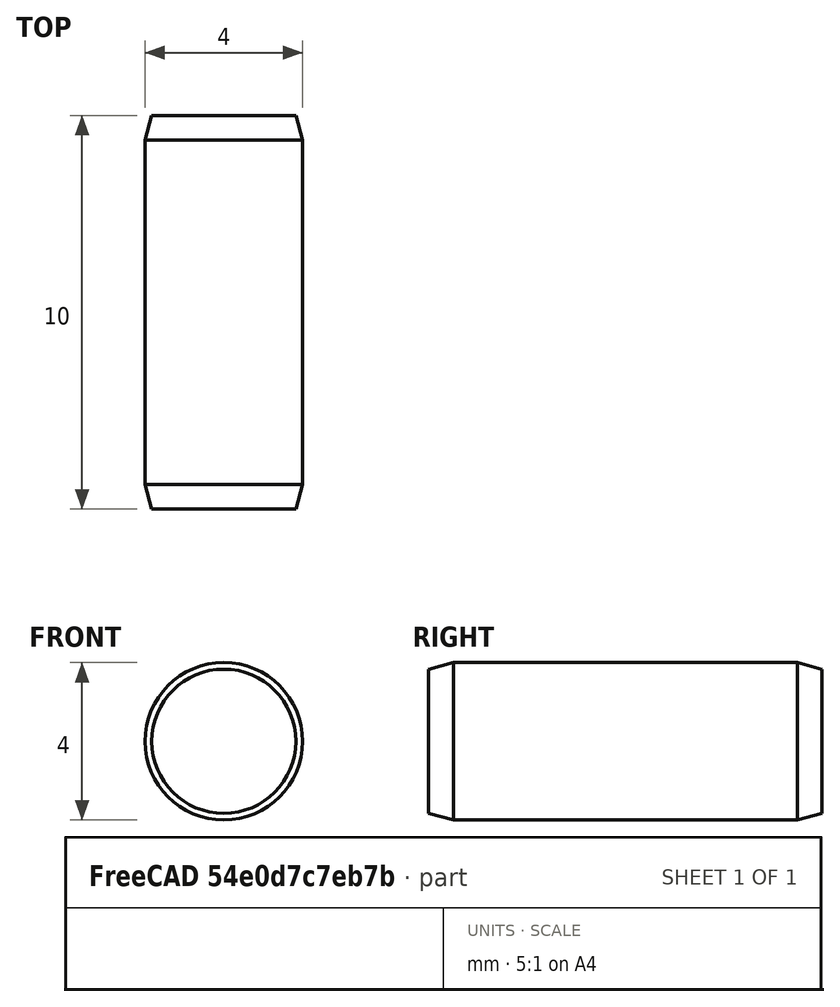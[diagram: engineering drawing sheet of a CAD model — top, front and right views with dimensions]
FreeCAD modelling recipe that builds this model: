
FCSTD DOCUMENT  (FreeCAD 0.15R4470 (Git))
Label: Zyl-Stift_ISO_8734-4x10
License: CC-BY 3.0
LicenseURL: http://creativecommons.org/licenses/by/3.0/
objects: Sketcher::SketchObject×1, PartDesign::Revolution×1
note: 3 computed .brp shape members not serialized (recipe doc carries the construction recipe); baked Part::Feature solids carry a one-line shape summary decoded from their .brp

FEATURE [Sketcher::SketchObject] Sketch
  Placement = pos=(0,0,0) rot=(0.57735,0.57735,0.57735;2.0944rad)
  sketch-geometry (7):
    g0: LineSegment StartX=0 StartY=0 StartZ=0 EndX=0 EndY=1.83119 EndZ=0
    g1: LineSegment StartX=0 StartY=1.83119 StartZ=0 EndX=0.63 EndY=2 EndZ=0
    g2: LineSegment StartX=0.63 StartY=2 StartZ=0 EndX=9.37 EndY=2 EndZ=0
    g3: LineSegment StartX=9.37 StartY=2 StartZ=0 EndX=10 EndY=1.83119 EndZ=0
    g4: LineSegment StartX=10 StartY=1.83119 StartZ=0 EndX=10 EndY=0 EndZ=0
    g5: LineSegment StartX=10 StartY=0 StartZ=0 EndX=0 EndY=0 EndZ=0
    g6: LineSegment [constr] StartX=0 StartY=1.83119 StartZ=0 EndX=10 EndY=1.83119 EndZ=0
  constraints (19):
    c: Coincident(g0,g-1)
    c: PointOnObject(g0,g-2)
    c: Coincident(g0,g1)
    c: Coincident(g1,g2)
    c: Horizontal(g2)
    c: Coincident(g2,g3)
    c: Coincident(g3,g4)
    c: Vertical(g4)
    c: Coincident(g4,g5)
    c: Coincident(g5,g-1)
    c: Horizontal(g5)
    c: Equal(g3,g1)
    c: Coincident(g6,g0)
    c: Coincident(g6,g3)
    c: Horizontal(g6)
    c: Angle(g6,g1) = 0.261799
    c: DistanceY(g-1,g1) = 2
    c: DistanceX(g5) = -10
    c: DistanceX(g1) = 0.63
FEATURE [PartDesign::Revolution] Revolution  label="Zyl-Stift ISO 8734-4x10 #"
  Angle = 360
  Axis = (0,1,0)
  Base = (0,0,0)
  Placement = pos=(0,0,0) rot=(0.57735,0.57735,0.57735;2.0944rad)
  ReferenceAxis = -> Sketch [H_Axis]
  Sketch = -> Sketch
